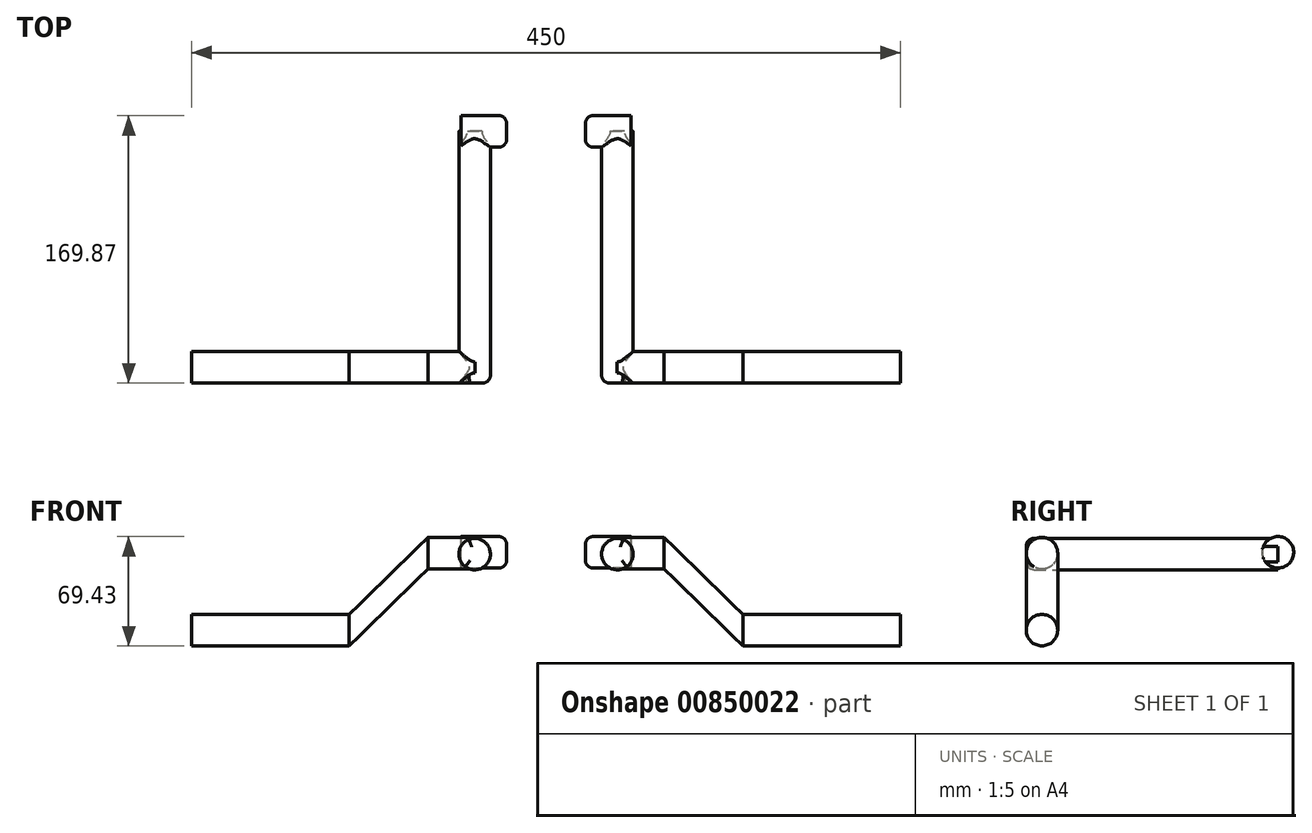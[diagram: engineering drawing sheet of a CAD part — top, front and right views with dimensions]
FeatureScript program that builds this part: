
annotation { "Feature Type Name" : "Feature", "Feature Type Description" : "" }
export const myFeature = defineFeature(function(context is Context, id is Id, definition is map)
    precondition{}
    {
        {
            var Q0;
            Q0=qCreatedBy(makeId("Right.planeOp"),FACE);
            var sketch = newSketch(context, id + "F0", { "sketchPlane" : qUnion([Q0])});
            skCircle(sketch, "E0", {"center": v(0, 0) * mm, "radius": 10 * mm});
            skSolve(sketch);
        }
        {
            var Q0;
            Q0=qSketchRegion(id+"F0",true);
            extrude(context, id + "F1", {"entities" : qUnion([Q0]), "depth" : 100 * mm, "offsetDistance" : 25 * mm});
        }
        {
            var Q0;
            Q0=qCreatedBy(makeId("Right.planeOp"),FACE);
            cPlane(context, id + "F2", {"entities" : qUnion([Q0]), "cplaneType" : CPlaneType.OFFSET, "offset" : 30 * mm, "oppositeDirection" : true, "width" : 150 * mm, "height" : 150 * mm});
        }
        {
            var Q0;
            Q0=qCreatedBy(id+"F2.planeOp",FACE);
            cPlane(context, id + "F3", {"entities" : qUnion([Q0]), "cplaneType" : CPlaneType.OFFSET, "offset" : 20 * mm, "oppositeDirection" : true, "width" : 150 * mm, "height" : 150 * mm});
        }
        {
            var Q0;
            Q0=qCreatedBy(id+"F3.planeOp",FACE);
            var sketch = newSketch(context, id + "F4", { "sketchPlane" : qUnion([Q0])});
            skCircle(sketch, "E1", {"center": v(0, 48.93) * mm, "radius": 10 * mm});
            skSolve(sketch);
        }
        {
            var Q0;
            Q0=makeQuery(id+"F1.opExtrude","CAP_FACE",FACE,{"disambiguationData":[OSD([sQuery(id+"F0.wireOp",EDGE,"E0")])],"isStart":true});
            var Q1;
            Q1=makeQuery(id+"F4.imprint","IMPRINT",FACE,{"disambiguationData":[TD([[makeQuery(id+"F4.imprint","IMPRINT",EDGE,{"derivedFrom":sQuery(id+"F4.wireOp",EDGE,"E1")}),1.0]])]});
            loft(context, id + "F5", {"sheetProfilesArray" : [{ "sheetProfileEntities" : qUnion([Q0]) }, { "sheetProfileEntities" : qUnion([Q1]) }]});
        }
        {
            var Q0;
            Q0=makeQuery(id+"F5.opLoft","CAP_FACE",FACE,{"disambiguationData":[OSD([makeQuery(id+"F4.imprint","IMPRINT",FACE,{"disambiguationData":[TD([[makeQuery(id+"F4.imprint","IMPRINT",EDGE,{"derivedFrom":sQuery(id+"F4.wireOp",EDGE,"E1")}),1.0]])]})])],"isStart":true});
            extrude(context, id + "F6", {"entities" : qUnion([Q0]), "operationType" : NewBodyOperationType.ADD, "depth" : 30 * mm, "offsetDistance" : 25 * mm});
        }
        {
            var Q0;
            Q0=qCreatedBy(makeId("Front.planeOp"),FACE);
            cPlane(context, id + "F7", {"entities" : qUnion([Q0]), "cplaneType" : CPlaneType.OFFSET, "offset" : 150 * mm, "oppositeDirection" : true, "width" : 150 * mm, "height" : 150 * mm});
        }
        {
            var Q0;
            Q0=qCreatedBy(id+"F7.planeOp",FACE);
            var sketch = newSketch(context, id + "F8", { "sketchPlane" : qUnion([Q0])});
            skCircle(sketch, "E2", {"center": v(-79.68, 48.3) * mm, "radius": 10 * mm});
            skSolve(sketch);
        }
        {
            var Q0;
            Q0=makeQuery(id+"F8.imprint","IMPRINT",FACE,{"disambiguationData":[TD([[makeQuery(id+"F8.imprint","IMPRINT",EDGE,{"derivedFrom":sQuery(id+"F8.wireOp",EDGE,"E2")}),1.0]])]});
            extrude(context, id + "F9", {"entities" : qUnion([Q0]), "operationType" : NewBodyOperationType.ADD, "depth" : 160 * mm, "offsetDistance" : 25 * mm});
        }
        {
            var Q0;
            Q0=qCreatedBy(id+"F3.planeOp",FACE);
            cPlane(context, id + "F10", {"entities" : qUnion([Q0]), "cplaneType" : CPlaneType.OFFSET, "offset" : 50 * mm, "oppositeDirection" : true, "width" : 150 * mm, "height" : 150 * mm});
        }
        {
            var Q0;
            Q0=qCreatedBy(id+"F10.planeOp",FACE);
            var sketch = newSketch(context, id + "F11", { "sketchPlane" : qUnion([Q0])});
            skCircle(sketch, "E3", {"center": v(149.87, 49.43) * mm, "radius": 10 * mm});
            skSolve(sketch);
        }
        {
            var Q0;
            Q0=makeQuery(id+"F11.imprint","IMPRINT",FACE,{"disambiguationData":[TD([[makeQuery(id+"F11.imprint","IMPRINT",EDGE,{"derivedFrom":sQuery(id+"F11.wireOp",EDGE,"E3")}),1.0]])]});
            extrude(context, id + "F12", {"entities" : qUnion([Q0]), "operationType" : NewBodyOperationType.ADD, "depth" : 29 * mm, "offsetDistance" : 25 * mm});
        }
        {
            var Q0;
            Q0=makeQuery(id+"F9.opExtrude","CAP_FACE",FACE,{"disambiguationData":[OSD([sQuery(id+"F8.wireOp",EDGE,"E2")])],"isStart":false});
            var Q1;
            Q1=makeQuery(id+"F12.opExtrude","CAP_EDGE",EDGE,{"disambiguationData":[OSD([sQuery(id+"F11.wireOp",EDGE,"E3")])],"isStart":true});
            fillet(context, id + "F13", {"entities" : qUnion([Q0, Q1]), "radius" : 5 * mm, "tangentPropagation" : true, "allowEdgeOverflow" : false});
        }
        {
            var Q0;
            Q0=qCreatedBy(id+"F10.planeOp",FACE);
            cPlane(context, id + "F14", {"entities" : qUnion([Q0]), "cplaneType" : CPlaneType.OFFSET, "offset" : 25 * mm, "oppositeDirection" : true, "width" : 150 * mm, "height" : 150 * mm});
        }
        {
            var Q0;
            Q0=makeQuery(id+"F1.opExtrude","SWEPT_BODY",BODY,{"disambiguationData":[OSD([sQuery(id+"F0.wireOp",EDGE,"E0")])]});
            var Q1;
            Q1=makeQuery(id+"F5.opLoft","SWEPT_BODY",BODY,{"disambiguationData":[OSD([sQuery(id+"F0.wireOp",EDGE,"E0"),makeQuery(id+"F4.imprint","IMPRINT",FACE,{"disambiguationData":[TD([[makeQuery(id+"F4.imprint","IMPRINT",EDGE,{"derivedFrom":sQuery(id+"F4.wireOp",EDGE,"E1")}),1.0]])]})])]});
            var Q2;
            Q2=qCreatedBy(id+"F14.planeOp",FACE);
            mirror(context, id + "F15", {"entities" : qUnion([Q0, Q1]), "mirrorPlane" : qUnion([Q2])});
        }
    });
